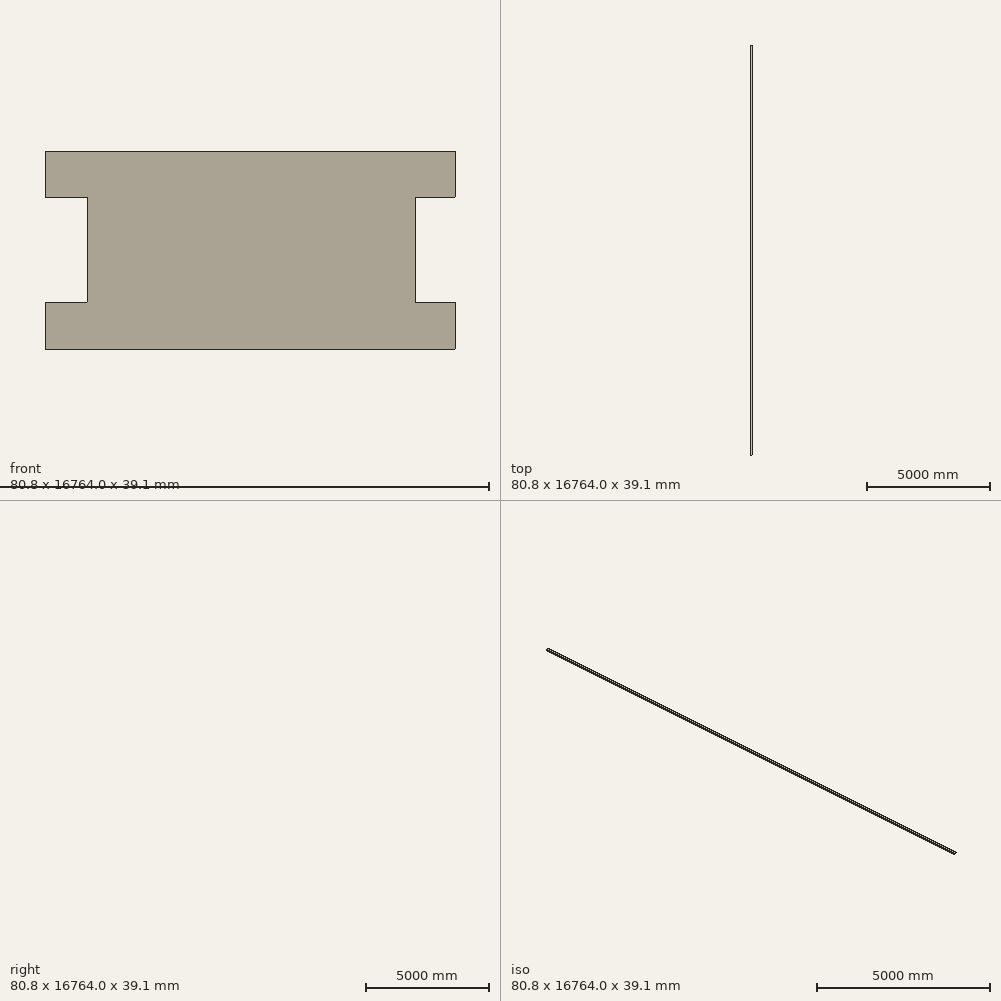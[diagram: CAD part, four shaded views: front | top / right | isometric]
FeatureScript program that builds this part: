
annotation { "Feature Type Name" : "Feature", "Feature Type Description" : "" }
export const myFeature = defineFeature(function(context is Context, id is Id, definition is map)
    precondition{}
    {
        {
            var Q0;
            Q0=qCreatedBy(makeId("Front.planeOp"),FACE);
            var sketch = newSketch(context, id + "F0", { "sketchPlane" : qUnion([Q0])});
            skLineSegment(sketch, "E0.bottom", {"start": v(-30.46, 25.67) * mm, "end": v(34.02, 25.67) * mm});
            skLineSegment(sketch, "E0.top", {"start": v(-30.46, -13.42) * mm, "end": v(34.02, -13.42) * mm});
            skLineSegment(sketch, "E0.left", {"start": v(-30.46, 25.67) * mm, "end": v(-30.46, -13.42) * mm});
            skLineSegment(sketch, "E0.right", {"start": v(34.02, 25.67) * mm, "end": v(34.02, -13.42) * mm});
            skLineSegment(sketch, "E1.bottom", {"start": v(34.02, -13.42) * mm, "end": v(41.97, -13.42) * mm});
            skLineSegment(sketch, "E1.top", {"start": v(34.02, -4.2) * mm, "end": v(41.97, -4.2) * mm});
            skLineSegment(sketch, "E1.left", {"start": v(34.02, -13.42) * mm, "end": v(34.02, -4.2) * mm});
            skLineSegment(sketch, "E1.right", {"start": v(41.97, -13.42) * mm, "end": v(41.97, -4.2) * mm});
            skLineSegment(sketch, "E2.bottom", {"start": v(-30.46, 25.67) * mm, "end": v(-38.8, 25.67) * mm});
            skLineSegment(sketch, "E2.top", {"start": v(-30.46, 16.67) * mm, "end": v(-38.8, 16.67) * mm});
            skLineSegment(sketch, "E2.left", {"start": v(-30.46, 25.67) * mm, "end": v(-30.46, 16.67) * mm});
            skLineSegment(sketch, "E2.right", {"start": v(-38.8, 25.67) * mm, "end": v(-38.8, 16.67) * mm});
            skPoint(sketch, "E3.oppositeSnap0", {"position": v(-34.63, 16.67) * mm});
            skLineSegment(sketch, "E3.bottom", {"start": v(34.02, 25.67) * mm, "end": v(41.97, 25.67) * mm});
            skLineSegment(sketch, "E3.top", {"start": v(34.02, 16.67) * mm, "end": v(41.97, 16.67) * mm});
            skLineSegment(sketch, "E3.left", {"start": v(34.02, 25.67) * mm, "end": v(34.02, 16.67) * mm});
            skLineSegment(sketch, "E3.right", {"start": v(41.97, 25.67) * mm, "end": v(41.97, 16.67) * mm});
            skLineSegment(sketch, "E4.bottom", {"start": v(-30.46, -13.42) * mm, "end": v(-38.8, -13.42) * mm});
            skLineSegment(sketch, "E4.top", {"start": v(-30.46, -4.2) * mm, "end": v(-38.8, -4.2) * mm});
            skLineSegment(sketch, "E4.left", {"start": v(-30.46, -13.42) * mm, "end": v(-30.46, -4.2) * mm});
            skLineSegment(sketch, "E4.right", {"start": v(-38.8, -13.42) * mm, "end": v(-38.8, -4.2) * mm});
            skLineSegment(sketch, "E5", {"start": v(-30.46, 25.67) * mm, "end": v(-21.98, 56.15) * mm});
            skLineSegment(sketch, "E6", {"start": v(34.02, 25.67) * mm, "end": v(26, 56.15) * mm});
            skSolve(sketch);
        }
        {
            var Q0;
            Q0 = qSketchRegion(id + "F0", true);
            extrude(context, id + "F1", {"entities" : qUnion([Q0]), "depth" : 16764 * mm});
        }
    });
